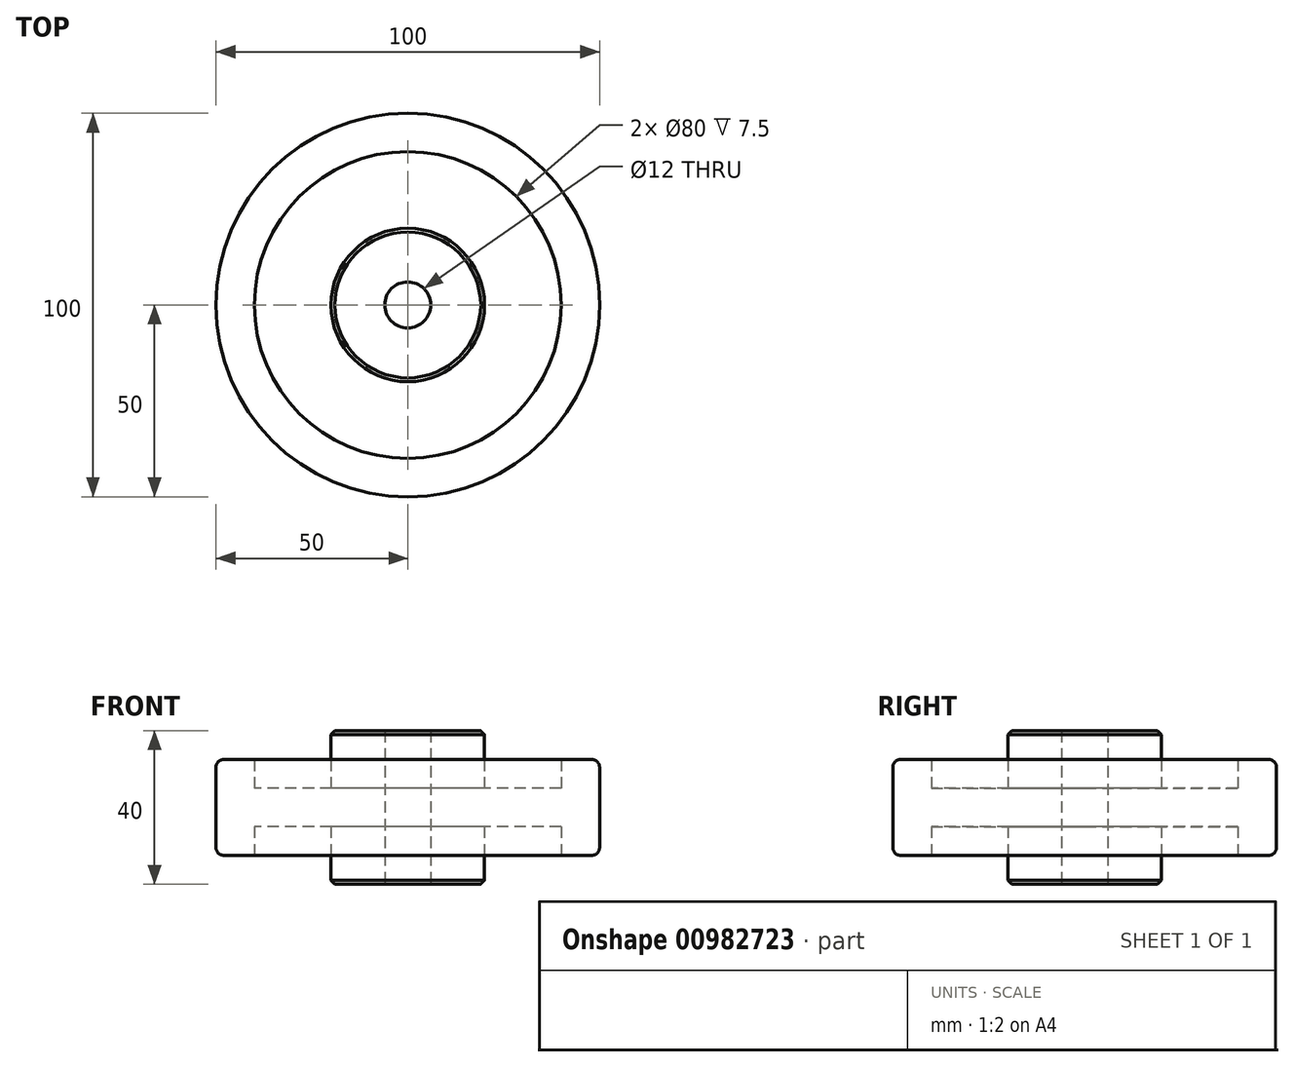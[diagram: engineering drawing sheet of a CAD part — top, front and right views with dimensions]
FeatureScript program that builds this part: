
annotation { "Feature Type Name" : "Feature", "Feature Type Description" : "" }
export const myFeature = defineFeature(function(context is Context, id is Id, definition is map)
    precondition{}
    {
        {
            var Q0;
            Q0=qCreatedBy(makeId("Top.planeOp"),FACE);
            var sketch = newSketch(context, id + "F0", { "sketchPlane" : qUnion([Q0])});
            skCircle(sketch, "E0", {"center": v(0, 0) * mm, "radius": 50 * mm});
            skCircle(sketch, "E1", {"center": v(0, 0) * mm, "radius": 40 * mm});
            skCircle(sketch, "E2", {"center": v(0, 0) * mm, "radius": 20 * mm});
            skCircle(sketch, "E3", {"center": v(0, 0) * mm, "radius": 6 * mm});
            skSolve(sketch);
        }
        {
            var Q0;
            Q0=makeQuery(id+"F0.imprint","IMPRINT",FACE,{"disambiguationData":[TD([[makeQuery(id+"F0.imprint","IMPRINT",EDGE,{"derivedFrom":sQuery(id+"F0.wireOp",EDGE,"E2")}),1.0]])]});
            extrude(context, id + "F1", {"entities" : qUnion([Q0]), "flatOperationType" : FlatOperationType.REMOVE, "depth" : 20 * mm, "offsetDistance" : 25 * mm, "hasSecondDirection" : true, "secondDirectionOppositeDirection" : true, "secondDirectionDepth" : 20 * mm, "domain" : OperationDomain.MODEL});
        }
        {
            var Q0;
            Q0=makeQuery(id+"F0.imprint","IMPRINT",FACE,{"disambiguationData":[TD([[makeQuery(id+"F0.imprint","IMPRINT",EDGE,{"derivedFrom":sQuery(id+"F0.wireOp",EDGE,"E1")}),1.0]])]});
            extrude(context, id + "F2", {"entities" : qUnion([Q0]), "operationType" : NewBodyOperationType.ADD, "depth" : 5 * mm, "offsetDistance" : 25 * mm, "hasSecondDirection" : true, "secondDirectionOppositeDirection" : true, "secondDirectionDepth" : 5 * mm});
        }
        {
            var Q0;
            Q0=makeQuery(id+"F0.imprint","IMPRINT",FACE,{"disambiguationData":[TD([[makeQuery(id+"F0.imprint","IMPRINT",EDGE,{"derivedFrom":sQuery(id+"F0.wireOp",EDGE,"E0")}),1.0]])]});
            extrude(context, id + "F3", {"entities" : qUnion([Q0]), "operationType" : NewBodyOperationType.ADD, "depth" : 12.5 * mm, "offsetDistance" : 25 * mm, "hasSecondDirection" : true, "secondDirectionOppositeDirection" : true, "secondDirectionDepth" : 12.5 * mm});
        }
        {
            var Q0;
            Q0=makeQuery(id+"F3.opExtrude","CAP_EDGE",EDGE,{"disambiguationData":[OSD([sQuery(id+"F0.wireOp",EDGE,"E0")])],"isStart":false});
            var Q1;
            Q1=makeQuery(id+"F3.opExtrude","CAP_EDGE",EDGE,{"disambiguationData":[OSD([sQuery(id+"F0.wireOp",EDGE,"E0")])],"isStart":true});
            fillet(context, id + "F4", {"entities" : qUnion([Q0, Q1]), "radius" : 2 * mm, "tangentPropagation" : true, "allowEdgeOverflow" : false});
        }
        {
            var Q0;
            Q0=makeQuery(id+"F1.opExtrude","CAP_EDGE",EDGE,{"disambiguationData":[OSD([sQuery(id+"F0.wireOp",EDGE,"E2")])],"isStart":false});
            var Q1;
            Q1=makeQuery(id+"F1.opExtrude","CAP_EDGE",EDGE,{"disambiguationData":[OSD([sQuery(id+"F0.wireOp",EDGE,"E2")])],"isStart":true});
            chamfer(context, id + "F5", {"entities" : qUnion([Q0, Q1]), "width" : 1 * mm, "tangentPropagation" : true});
        }
    });
